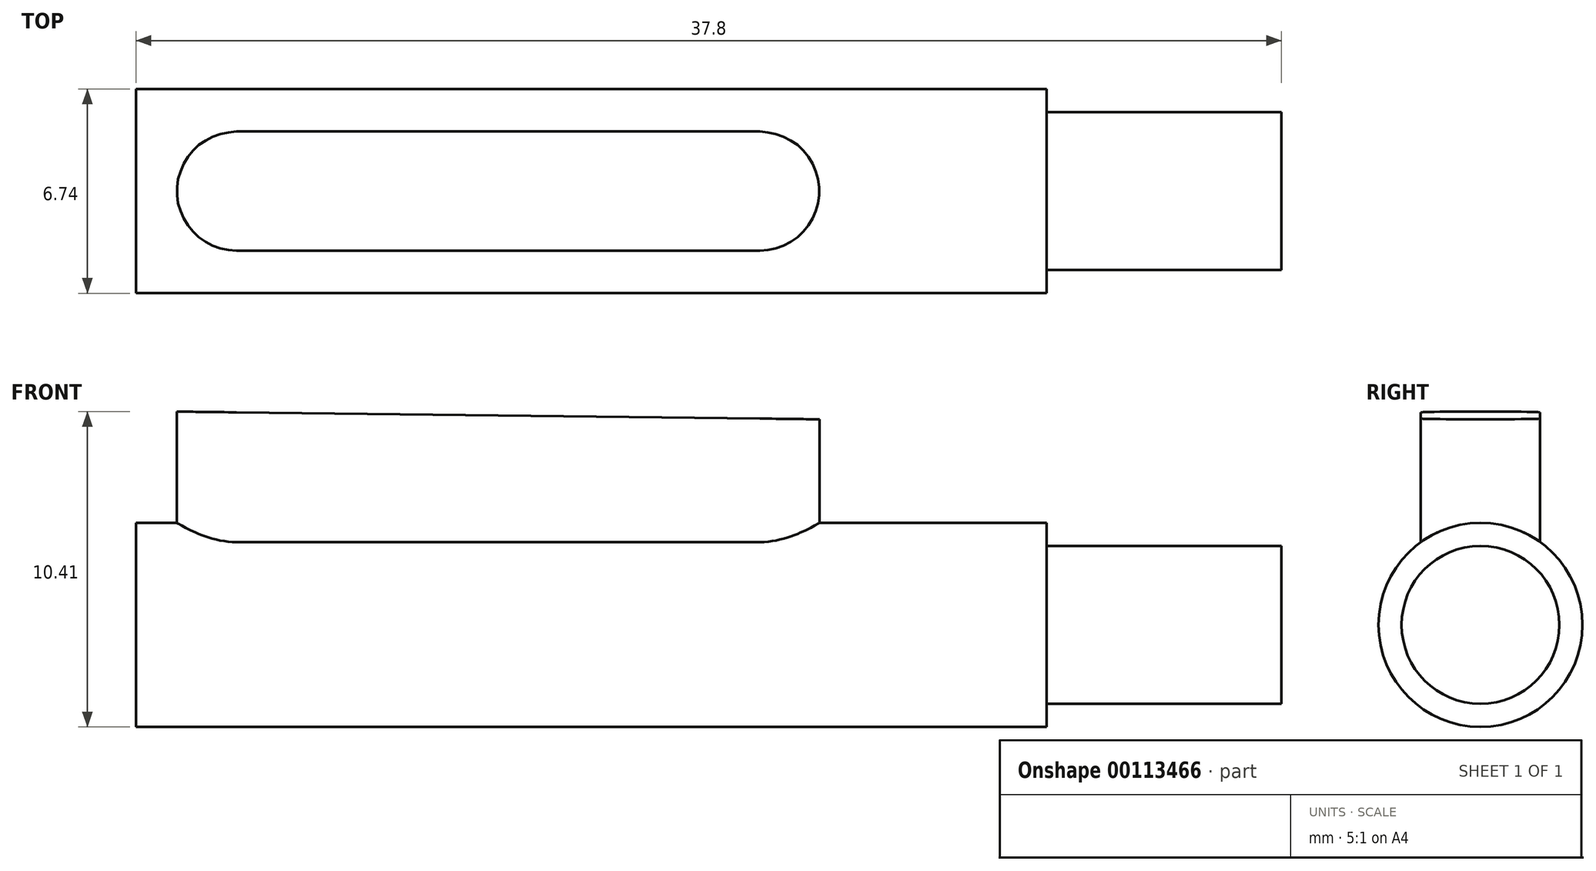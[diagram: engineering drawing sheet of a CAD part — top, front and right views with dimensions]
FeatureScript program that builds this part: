
annotation { "Feature Type Name" : "Feature", "Feature Type Description" : "" }
export const myFeature = defineFeature(function(context is Context, id is Id, definition is map)
    precondition{}
    {
        {
            var Q0;
            Q0=qCreatedBy(makeId("Right.planeOp"),FACE);
            var sketch = newSketch(context, id + "F0", { "sketchPlane" : qUnion([Q0])});
            skCircle(sketch, "E0", {"center": v(0, 0) * mm, "radius": 3.37 * mm});
            skSolve(sketch);
        }
        {
            var Q0;
            Q0 = qSketchRegion(id + "F0", true);
            extrude(context, id + "F1", {"entities" : qUnion([Q0]), "oppositeDirection" : true, "depth" : 30.05 * mm});
        }
        {
            var Q0;
            Q0=makeQuery(id+"F1.opExtrude","CAP_FACE",FACE,{"disambiguationData":[OSD([sQuery(id+"F0.wireOp",EDGE,"E0")])],"isStart":true});
            var sketch = newSketch(context, id + "F2", { "sketchPlane" : qUnion([Q0])});
            skCircle(sketch, "E1", {"center": v(0, 0) * mm, "radius": 2.6 * mm});
            skSolve(sketch);
        }
        {
            var Q0;
            Q0 = qSketchRegion(id + "F2", true);
            extrude(context, id + "F3", {"entities" : qUnion([Q0]), "operationType" : NewBodyOperationType.ADD, "depth" : 7.75 * mm});
        }
        {
            var Q0;
            Q0=qCreatedBy(makeId("Top.planeOp"),FACE);
            var sketch = newSketch(context, id + "F4", { "sketchPlane" : qUnion([Q0])});
            skLineSegment(sketch, "E2", {"start": v(-26.73, 1.97) * mm, "end": v(-9.46, 1.97) * mm});
            skArc(sketch, "E3", {"start": v(-9.46, -1.97) * mm, "mid": v(-7.5, 0) * mm, "end": v(-9.46, 1.97) * mm});
            skArc(sketch, "E4", {"start": v(-26.73, 1.97) * mm, "mid": v(-28.7, 0) * mm, "end": v(-26.73, -1.97) * mm});
            skLineSegment(sketch, "E5", {"start": v(-26.73, -1.97) * mm, "end": v(-9.46, -1.97) * mm});
            skLineSegment(sketch, "E6", {"start": v(-26.73, 0) * mm, "end": v(-9.46, 0) * mm, "construction": true});
            skSolve(sketch);
        }
        {
            var Q0;
            Q0 = qSketchRegion(id + "F4", true);
            extrude(context, id + "F5", {"entities" : qUnion([Q0]), "operationType" : NewBodyOperationType.ADD, "depth" : 7.04 * mm});
        }
        {
            var Q0;
            Q0=makeQuery(id+"F5.opExtrude","SWEPT_FACE",FACE,{"disambiguationData":[OSD([sQuery(id+"F4.wireOp",EDGE,"E5")])]});
            var sketch = newSketch(context, id + "F6", { "sketchPlane" : qUnion([Q0])});
            skLineSegment(sketch, "E7", {"start": v(-28.7, 7.04) * mm, "end": v(-7.5, 6.78) * mm});
            skLineSegment(sketch, "E8", {"start": v(-7.5, 6.78) * mm, "end": v(-7.5, 7.04) * mm});
            skLineSegment(sketch, "E9", {"start": v(-7.5, 7.04) * mm, "end": v(-28.7, 7.04) * mm});
            skSolve(sketch);
        }
        {
            var Q0;
            Q0 = qSketchRegion(id + "F6", true);
            extrude(context, id + "F7", {"entities" : qUnion([Q0]), "operationType" : NewBodyOperationType.REMOVE, "endBound" : BoundingType.THROUGH_ALL, "oppositeDirection" : true, "depth" : 25.4 * mm});
        }
    });
